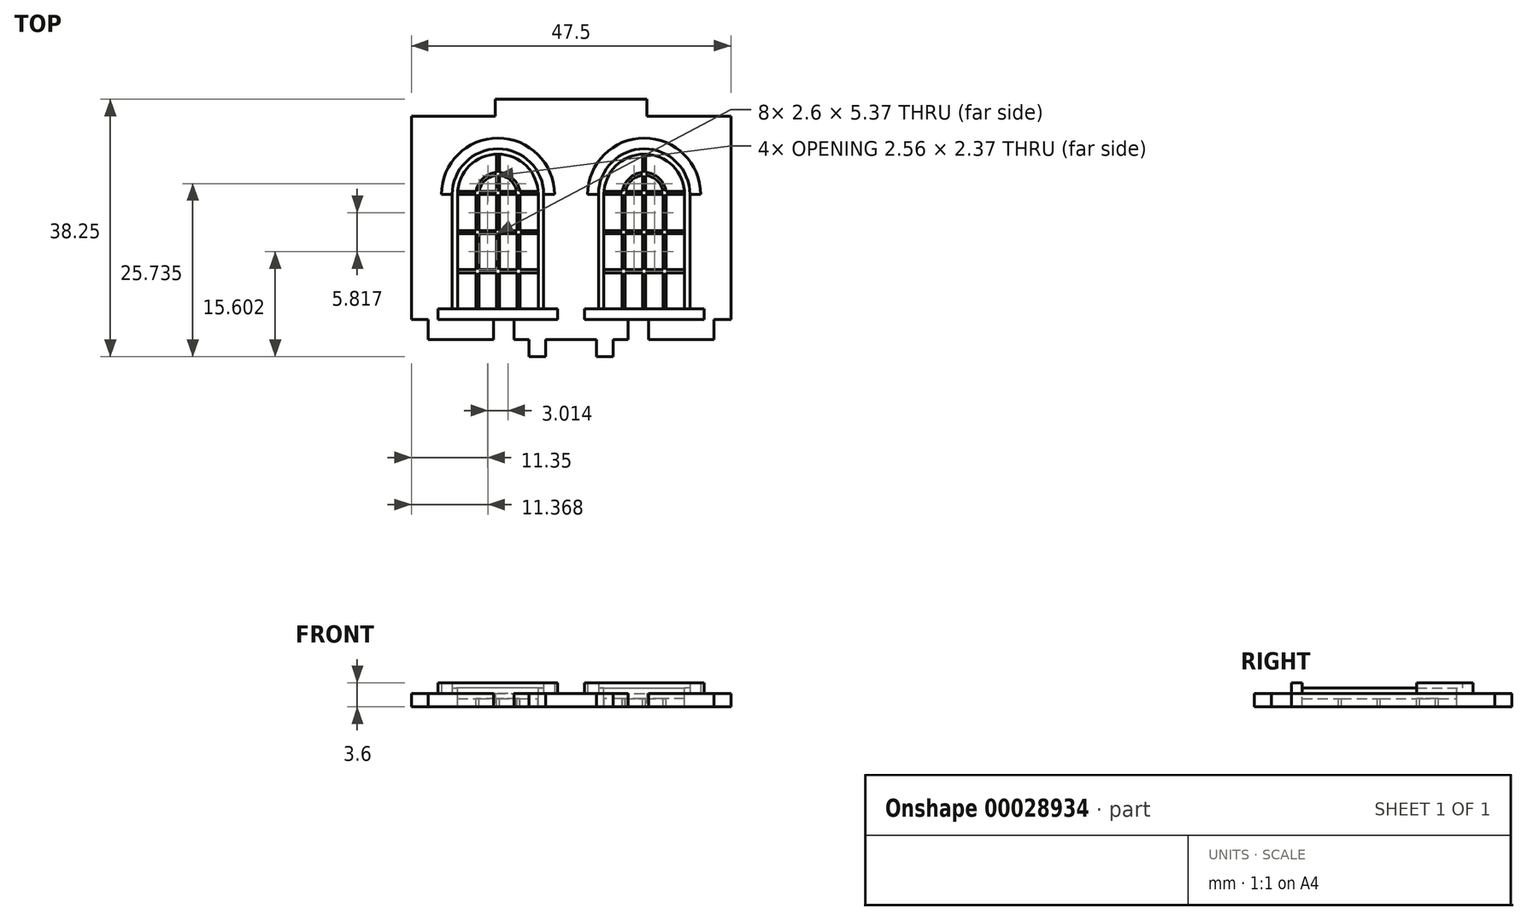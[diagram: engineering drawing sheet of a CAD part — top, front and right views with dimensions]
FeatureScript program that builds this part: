
annotation { "Feature Type Name" : "Feature", "Feature Type Description" : "" }
export const myFeature = defineFeature(function(context is Context, id is Id, definition is map)
    precondition{}
    {
        {
            var Q0;
            Q0=qCreatedBy(makeId("Top.planeOp"),FACE);
            var sketch = newSketch(context, id + "F0", { "sketchPlane" : qUnion([Q0])});
            skLineSegment(sketch, "E0.bottom", {"start": v(-8.5, -5.78) * mm, "end": v(-11.5, -5.78) * mm});
            skLineSegment(sketch, "E0.top", {"start": v(-11.25, 24.47) * mm, "end": v(-23.75, 24.47) * mm});
            skLineSegment(sketch, "E0.right", {"start": v(-23.75, -5.78) * mm, "end": v(-23.75, 24.47) * mm});
            skLineSegment(sketch, "E1.top", {"start": v(-11.25, 26.97) * mm, "end": v(0, 26.97) * mm});
            skLineSegment(sketch, "E1.left", {"start": v(-11.25, 24.47) * mm, "end": v(-11.25, 26.97) * mm});
            skLineSegment(sketch, "E1.right", {"start": v(0, -8.78) * mm, "end": v(0, 26.97) * mm});
            skLineSegment(sketch, "E2.top", {"start": v(-21.25, -8.78) * mm, "end": v(-11.5, -8.78) * mm});
            skLineSegment(sketch, "E2.left", {"start": v(-21.25, -5.78) * mm, "end": v(-21.25, -8.78) * mm});
            skLineSegment(sketch, "E2.right", {"start": v(-11.5, -5.78) * mm, "end": v(-11.5, -8.78) * mm});
            skLineSegment(sketch, "E3.top", {"start": v(-8.5, -8.78) * mm, "end": v(-6.25, -8.78) * mm});
            skLineSegment(sketch, "E3.left", {"start": v(-8.5, -5.78) * mm, "end": v(-8.5, -8.78) * mm});
            skLineSegment(sketch, "E4.top", {"start": v(-6.25, -11.28) * mm, "end": v(-3.75, -11.28) * mm});
            skLineSegment(sketch, "E4.left", {"start": v(-6.25, -8.78) * mm, "end": v(-6.25, -11.28) * mm});
            skLineSegment(sketch, "E4.right", {"start": v(-3.75, -8.78) * mm, "end": v(-3.75, -11.28) * mm});
            skLineSegment(sketch, "E5.trimOffspring", {"start": v(-3.75, -8.78) * mm, "end": v(0, -8.78) * mm});
            skLineSegment(sketch, "E6.trimOffspring", {"start": v(-21.25, -5.78) * mm, "end": v(-23.75, -5.78) * mm});
            skLineSegment(sketch, "E7.MirrorCS", {"start": v(11.25, 26.97) * mm, "end": v(0, 26.97) * mm});
            skLineSegment(sketch, "E8.MirrorCS", {"start": v(11.25, 24.47) * mm, "end": v(11.25, 26.97) * mm});
            skLineSegment(sketch, "E9.MirrorCS", {"start": v(11.25, 24.47) * mm, "end": v(23.75, 24.47) * mm});
            skLineSegment(sketch, "E10.MirrorCS", {"start": v(23.75, -5.78) * mm, "end": v(23.75, 24.47) * mm});
            skLineSegment(sketch, "E11.MirrorCS", {"start": v(21.25, -5.78) * mm, "end": v(23.75, -5.78) * mm});
            skLineSegment(sketch, "E12.MirrorCS", {"start": v(21.25, -5.78) * mm, "end": v(21.25, -8.78) * mm});
            skLineSegment(sketch, "E13.MirrorCS", {"start": v(21.25, -8.78) * mm, "end": v(11.5, -8.78) * mm});
            skLineSegment(sketch, "E14.MirrorCS", {"start": v(11.5, -5.78) * mm, "end": v(11.5, -8.78) * mm});
            skLineSegment(sketch, "E15.MirrorCS", {"start": v(8.5, -5.78) * mm, "end": v(11.5, -5.78) * mm});
            skLineSegment(sketch, "E16.MirrorCS", {"start": v(8.5, -5.78) * mm, "end": v(8.5, -8.78) * mm});
            skLineSegment(sketch, "E17.MirrorCS", {"start": v(8.5, -8.78) * mm, "end": v(6.25, -8.78) * mm});
            skLineSegment(sketch, "E18.MirrorCS", {"start": v(6.25, -8.78) * mm, "end": v(6.25, -11.28) * mm});
            skLineSegment(sketch, "E19.MirrorCS", {"start": v(6.25, -11.28) * mm, "end": v(3.75, -11.28) * mm});
            skLineSegment(sketch, "E20.MirrorCS", {"start": v(3.75, -8.78) * mm, "end": v(3.75, -11.28) * mm});
            skLineSegment(sketch, "E21.MirrorCS", {"start": v(3.75, -8.78) * mm, "end": v(0, -8.78) * mm});
            skSolve(sketch);
        }
        {
            var Q0;
            Q0=makeQuery(id+"F0.imprint","IMPRINT",FACE,{"disambiguationData":[TD([[makeQuery(id+"F0.imprint","IMPRINT",EDGE,{"derivedFrom":sQuery(id+"F0.wireOp",EDGE,"E0.bottom")}),-1.0]])]});
            extrude(context, id + "F1", {"entities" : qUnion([Q0]), "depth" : 2 * mm});
        }
        {
            var Q0;
            Q0=makeQuery(id+"F1.opExtrude","CAP_FACE",FACE,{"disambiguationData":[OSD([sQuery(id+"F0.wireOp",EDGE,"E0.bottom"),sQuery(id+"F0.wireOp",EDGE,"E0.top"),sQuery(id+"F0.wireOp",EDGE,"E0.right"),sQuery(id+"F0.wireOp",EDGE,"E1.top"),sQuery(id+"F0.wireOp",EDGE,"E1.left"),sQuery(id+"F0.wireOp",EDGE,"E2.top"),sQuery(id+"F0.wireOp",EDGE,"E2.left"),sQuery(id+"F0.wireOp",EDGE,"E2.right"),sQuery(id+"F0.wireOp",EDGE,"E3.top"),sQuery(id+"F0.wireOp",EDGE,"E3.left"),sQuery(id+"F0.wireOp",EDGE,"E4.top"),sQuery(id+"F0.wireOp",EDGE,"E4.left"),sQuery(id+"F0.wireOp",EDGE,"E4.right"),sQuery(id+"F0.wireOp",EDGE,"E5.trimOffspring"),sQuery(id+"F0.wireOp",EDGE,"E6.trimOffspring"),sQuery(id+"F0.wireOp",EDGE,"E7.MirrorCS"),sQuery(id+"F0.wireOp",EDGE,"E8.MirrorCS"),sQuery(id+"F0.wireOp",EDGE,"E9.MirrorCS"),sQuery(id+"F0.wireOp",EDGE,"E10.MirrorCS"),sQuery(id+"F0.wireOp",EDGE,"E11.MirrorCS"),sQuery(id+"F0.wireOp",EDGE,"E12.MirrorCS"),sQuery(id+"F0.wireOp",EDGE,"E13.MirrorCS"),sQuery(id+"F0.wireOp",EDGE,"E14.MirrorCS"),sQuery(id+"F0.wireOp",EDGE,"E15.MirrorCS"),sQuery(id+"F0.wireOp",EDGE,"E16.MirrorCS"),sQuery(id+"F0.wireOp",EDGE,"E17.MirrorCS"),sQuery(id+"F0.wireOp",EDGE,"E18.MirrorCS"),sQuery(id+"F0.wireOp",EDGE,"E19.MirrorCS"),sQuery(id+"F0.wireOp",EDGE,"E20.MirrorCS"),sQuery(id+"F0.wireOp",EDGE,"E21.MirrorCS")])],"isStart":false});
            var sketch = newSketch(context, id + "F2", { "sketchPlane" : qUnion([Q0])});
            skLineSegment(sketch, "E22.bottom", {"start": v(-19.75, -5.78) * mm, "end": v(-2, -5.78) * mm});
            skLineSegment(sketch, "E22.top", {"start": v(-19.75, -4.18) * mm, "end": v(-2, -4.18) * mm});
            skLineSegment(sketch, "E22.left", {"start": v(-19.75, -5.78) * mm, "end": v(-19.75, -4.18) * mm});
            skLineSegment(sketch, "E22.right", {"start": v(-2, -5.78) * mm, "end": v(-2, -4.18) * mm});
            skLineSegment(sketch, "E23", {"start": v(-16.87, -4.18) * mm, "end": v(-16.87, 1.19) * mm});
            skLineSegment(sketch, "E24", {"start": v(-4.87, -4.18) * mm, "end": v(-4.87, 12.82) * mm});
            skArc(sketch, "E25", {"start": v(-4.87, 12.82) * mm, "mid": v(-10.87, 18.82) * mm, "end": v(-16.88, 12.82) * mm});
            skLineSegment(sketch, "E26", {"start": v(-10.88, 12.82) * mm, "end": v(-10.87, 1.64) * mm, "construction": true});
            skLineSegment(sketch, "E27.0", {"start": v(-4.07, -4.18) * mm, "end": v(-4.08, 12.82) * mm});
            skArc(sketch, "E27.1", {"start": v(-4.08, 12.82) * mm, "mid": v(-10.88, 19.62) * mm, "end": v(-17.67, 12.82) * mm});
            skLineSegment(sketch, "E27.2", {"start": v(-17.67, -4.18) * mm, "end": v(-17.67, 12.82) * mm});
            skArc(sketch, "E28.0", {"start": v(-2.47, 12.82) * mm, "mid": v(-10.88, 21.22) * mm, "end": v(-19.28, 12.82) * mm});
            skLineSegment(sketch, "E29", {"start": v(-19.28, 12.82) * mm, "end": v(-17.67, 12.82) * mm});
            skLineSegment(sketch, "E30", {"start": v(-4.08, 12.82) * mm, "end": v(-2.47, 12.82) * mm});
            skLineSegment(sketch, "E31", {"start": v(-13.7, -4.18) * mm, "end": v(-13.7, 1.19) * mm});
            skLineSegment(sketch, "E32", {"start": v(-8.05, -4.18) * mm, "end": v(-8.05, 1.19) * mm});
            skArc(sketch, "E33", {"start": v(-8.09, 13.27) * mm, "mid": v(-8.96, 14.9) * mm, "end": v(-10.65, 15.64) * mm});
            skLineSegment(sketch, "E34.0", {"start": v(-7.6, -4.18) * mm, "end": v(-7.6, 1.19) * mm});
            skArc(sketch, "E34.1", {"start": v(-7.63, 13.27) * mm, "mid": v(-8.64, 15.22) * mm, "end": v(-10.65, 16.09) * mm});
            skLineSegment(sketch, "E34.2", {"start": v(-14.15, -4.18) * mm, "end": v(-14.15, 1.19) * mm});
            skLineSegment(sketch, "E35", {"start": v(-11.1, -4.18) * mm, "end": v(-11.1, 1.19) * mm});
            skLineSegment(sketch, "E36", {"start": v(-10.65, 18.82) * mm, "end": v(-10.65, 16.09) * mm});
            skLineSegment(sketch, "E37", {"start": v(-16.86, 13.27) * mm, "end": v(-14.12, 13.27) * mm});
            skLineSegment(sketch, "E38", {"start": v(-16.87, 12.82) * mm, "end": v(-14.15, 12.82) * mm});
            skLineSegment(sketch, "E39.bottom", {"start": v(-16.87, 7) * mm, "end": v(-14.15, 7) * mm});
            skLineSegment(sketch, "E39.top", {"start": v(-16.87, 7.46) * mm, "end": v(-14.15, 7.46) * mm});
            skLineSegment(sketch, "E40.bottom", {"start": v(-16.87, 1.64) * mm, "end": v(-14.15, 1.64) * mm});
            skLineSegment(sketch, "E40.top", {"start": v(-16.87, 1.19) * mm, "end": v(-14.15, 1.19) * mm});
            skLineSegment(sketch, "E41.trimOffspring", {"start": v(-16.87, 7) * mm, "end": v(-16.87, 12.82) * mm});
            skLineSegment(sketch, "E42.trimOffspring", {"start": v(-14.15, 7.46) * mm, "end": v(-14.15, 12.82) * mm});
            skLineSegment(sketch, "E43.trimOffspring", {"start": v(-13.7, 7.46) * mm, "end": v(-13.7, 12.82) * mm});
            skLineSegment(sketch, "E44.trimOffspring", {"start": v(-13.7, 7) * mm, "end": v(-11.1, 7) * mm});
            skLineSegment(sketch, "E45.trimOffspring", {"start": v(-13.7, 7.46) * mm, "end": v(-11.1, 7.46) * mm});
            skLineSegment(sketch, "E46.trimOffspring", {"start": v(-8.05, 7.46) * mm, "end": v(-8.05, 12.82) * mm});
            skLineSegment(sketch, "E47.trimOffspring", {"start": v(-7.6, 7) * mm, "end": v(-4.88, 7) * mm});
            skLineSegment(sketch, "E48.trimOffspring", {"start": v(-7.6, 7.46) * mm, "end": v(-7.6, 12.82) * mm});
            skLineSegment(sketch, "E49.trimOffspring", {"start": v(-7.6, 7.46) * mm, "end": v(-4.88, 7.46) * mm});
            skLineSegment(sketch, "E50.trimOffspring", {"start": v(-7.6, 12.82) * mm, "end": v(-4.88, 12.82) * mm});
            skLineSegment(sketch, "E51.trimOffspring", {"start": v(-7.63, 13.27) * mm, "end": v(-4.9, 13.27) * mm});
            skLineSegment(sketch, "E52.trimOffspring", {"start": v(-13.7, 12.82) * mm, "end": v(-11.1, 12.82) * mm});
            skLineSegment(sketch, "E53.trimOffspring", {"start": v(-13.66, 13.27) * mm, "end": v(-11.1, 13.27) * mm});
            skLineSegment(sketch, "E54.trimOffspring", {"start": v(-11.1, 13.27) * mm, "end": v(-11.1, 15.64) * mm});
            skLineSegment(sketch, "E55.trimOffspring", {"start": v(-10.65, 13.27) * mm, "end": v(-8.09, 13.27) * mm});
            skLineSegment(sketch, "E56.trimOffspring", {"start": v(-10.65, 12.82) * mm, "end": v(-10.65, 7.46) * mm});
            skLineSegment(sketch, "E57.trimOffspring", {"start": v(-10.65, 12.82) * mm, "end": v(-8.05, 12.82) * mm});
            skArc(sketch, "E58.trimOffspring", {"start": v(-11.1, 15.64) * mm, "mid": v(-12.8, 14.9) * mm, "end": v(-13.66, 13.27) * mm});
            skArc(sketch, "E59.trimOffspring", {"start": v(-11.1, 16.09) * mm, "mid": v(-13.1, 15.22) * mm, "end": v(-14.12, 13.27) * mm});
            skLineSegment(sketch, "E60.trimOffspring", {"start": v(-11.1, 16.09) * mm, "end": v(-11.1, 18.82) * mm});
            skLineSegment(sketch, "E61.trimOffspring", {"start": v(-10.65, 15.64) * mm, "end": v(-10.65, 13.27) * mm});
            skLineSegment(sketch, "E62.trimOffspring", {"start": v(-13.7, 1.64) * mm, "end": v(-13.7, 7) * mm});
            skLineSegment(sketch, "E63.trimOffspring", {"start": v(-13.7, 1.64) * mm, "end": v(-11.1, 1.64) * mm});
            skLineSegment(sketch, "E64.trimOffspring", {"start": v(-14.15, 1.64) * mm, "end": v(-14.15, 7) * mm});
            skLineSegment(sketch, "E65.trimOffspring", {"start": v(-13.7, 1.19) * mm, "end": v(-11.1, 1.19) * mm});
            skLineSegment(sketch, "E66.trimOffspring", {"start": v(-10.65, 1.19) * mm, "end": v(-10.65, -4.18) * mm});
            skLineSegment(sketch, "E67.trimOffspring", {"start": v(-11.1, 1.64) * mm, "end": v(-11.1, 7) * mm});
            skLineSegment(sketch, "E68.trimOffspring", {"start": v(-10.87, 1.19) * mm, "end": v(-10.87, -4.18) * mm, "construction": true});
            skLineSegment(sketch, "E69.trimOffspring", {"start": v(-10.65, 1.64) * mm, "end": v(-8.05, 1.64) * mm});
            skLineSegment(sketch, "E70.trimOffspring", {"start": v(-10.65, 1.19) * mm, "end": v(-8.05, 1.19) * mm});
            skLineSegment(sketch, "E71.trimOffspring", {"start": v(-7.6, 1.64) * mm, "end": v(-4.88, 1.64) * mm});
            skLineSegment(sketch, "E72.trimOffspring", {"start": v(-8.05, 1.64) * mm, "end": v(-8.05, 7) * mm});
            skLineSegment(sketch, "E73.trimOffspring", {"start": v(-7.6, 1.19) * mm, "end": v(-4.88, 1.19) * mm});
            skLineSegment(sketch, "E74.trimOffspring", {"start": v(-7.6, 1.64) * mm, "end": v(-7.6, 7) * mm});
            skLineSegment(sketch, "E75", {"start": v(-16.87, 7.46) * mm, "end": v(-16.87, 7) * mm});
            skLineSegment(sketch, "E76.trimOffspring", {"start": v(-16.87, 1.64) * mm, "end": v(-16.87, 7.46) * mm});
            skLineSegment(sketch, "E77", {"start": v(-16.87, 1.64) * mm, "end": v(-16.87, 1.19) * mm});
            skLineSegment(sketch, "E78.trimOffspring", {"start": v(-10.65, 7) * mm, "end": v(-10.65, 1.64) * mm});
            skLineSegment(sketch, "E79.trimOffspring", {"start": v(-10.65, 7.46) * mm, "end": v(-8.05, 7.46) * mm});
            skLineSegment(sketch, "E80.trimOffspring", {"start": v(-10.65, 7) * mm, "end": v(-8.05, 7) * mm});
            skLineSegment(sketch, "E81.trimOffspring", {"start": v(-11.1, 7.46) * mm, "end": v(-11.1, 12.82) * mm});
            skSolve(sketch);
        }
        {
            var Q0;
            {var subQ1=sQuery(id+"F2.wireOp",EDGE,"E37");Q0=makeQuery(id+"F2.imprint","IMPRINT",FACE,{"disambiguationData":[TD([[makeQuery(id+"F2.imprint","IMPRINT",EDGE,{"derivedFrom":subQ1}),1.0]])]});}
            var Q1;
            Q1=makeQuery(id+"F2.imprint","IMPRINT",FACE,{"disambiguationData":[TD([[makeQuery(id+"F2.imprint","IMPRINT",EDGE,{"derivedFrom":sQuery(id+"F2.wireOp",EDGE,"E53.trimOffspring")}),1.0]])]});
            var Q2;
            Q2=makeQuery(id+"F2.imprint","IMPRINT",FACE,{"disambiguationData":[TD([[makeQuery(id+"F2.imprint","IMPRINT",EDGE,{"derivedFrom":sQuery(id+"F2.wireOp",EDGE,"E34.1")}),-1.0]])]});
            var Q3;
            Q3=makeQuery(id+"F2.imprint","IMPRINT",FACE,{"disambiguationData":[TD([[makeQuery(id+"F2.imprint","IMPRINT",EDGE,{"derivedFrom":sQuery(id+"F2.wireOp",EDGE,"E33")}),1.0]])]});
            var Q4;
            Q4=makeQuery(id+"F2.imprint","IMPRINT",FACE,{"disambiguationData":[TD([[makeQuery(id+"F2.imprint","IMPRINT",EDGE,{"derivedFrom":sQuery(id+"F2.wireOp",EDGE,"E48.trimOffspring")}),-1.0]])]});
            var Q5;
            Q5=makeQuery(id+"F2.imprint","IMPRINT",FACE,{"disambiguationData":[TD([[makeQuery(id+"F2.imprint","IMPRINT",EDGE,{"derivedFrom":sQuery(id+"F2.wireOp",EDGE,"E46.trimOffspring")}),1.0]])]});
            var Q6;
            Q6=makeQuery(id+"F2.imprint","IMPRINT",FACE,{"disambiguationData":[TD([[makeQuery(id+"F2.imprint","IMPRINT",EDGE,{"derivedFrom":sQuery(id+"F2.wireOp",EDGE,"E43.trimOffspring")}),-1.0]])]});
            var Q7;
            Q7=makeQuery(id+"F2.imprint","IMPRINT",FACE,{"disambiguationData":[TD([[makeQuery(id+"F2.imprint","IMPRINT",EDGE,{"derivedFrom":sQuery(id+"F2.wireOp",EDGE,"E38")}),-1.0]])]});
            var Q8;
            {var subQ2=sQuery(id+"F2.wireOp",EDGE,"E39.bottom");Q8=makeQuery(id+"F2.imprint","IMPRINT",FACE,{"disambiguationData":[TD([[makeQuery(id+"F2.imprint","IMPRINT",EDGE,{"derivedFrom":subQ2}),-1.0]])]});}
            var Q9;
            Q9=makeQuery(id+"F2.imprint","IMPRINT",FACE,{"disambiguationData":[TD([[makeQuery(id+"F2.imprint","IMPRINT",EDGE,{"derivedFrom":sQuery(id+"F2.wireOp",EDGE,"E44.trimOffspring")}),-1.0]])]});
            var Q10;
            Q10=makeQuery(id+"F2.imprint","IMPRINT",FACE,{"disambiguationData":[TD([[makeQuery(id+"F2.imprint","IMPRINT",EDGE,{"derivedFrom":sQuery(id+"F2.wireOp",EDGE,"E69.trimOffspring")}),1.0]])]});
            var Q11;
            {var subQ1=sQuery(id+"F2.wireOp",EDGE,"E47.trimOffspring");Q11=makeQuery(id+"F2.imprint","IMPRINT",FACE,{"disambiguationData":[TD([[makeQuery(id+"F2.imprint","IMPRINT",EDGE,{"derivedFrom":subQ1}),-1.0]])]});}
            var Q12;
            {var subQ1=sQuery(id+"F2.wireOp",EDGE,"E34.0");Q12=makeQuery(id+"F2.imprint","IMPRINT",FACE,{"disambiguationData":[TD([[makeQuery(id+"F2.imprint","IMPRINT",EDGE,{"derivedFrom":subQ1}),-1.0]])]});}
            var Q13;
            {var subQ1=sQuery(id+"F2.wireOp",EDGE,"E32");Q13=makeQuery(id+"F2.imprint","IMPRINT",FACE,{"disambiguationData":[TD([[makeQuery(id+"F2.imprint","IMPRINT",EDGE,{"derivedFrom":subQ1}),1.0]])]});}
            var Q14;
            {var subQ1=sQuery(id+"F2.wireOp",EDGE,"E31");Q14=makeQuery(id+"F2.imprint","IMPRINT",FACE,{"disambiguationData":[TD([[makeQuery(id+"F2.imprint","IMPRINT",EDGE,{"derivedFrom":subQ1}),-1.0]])]});}
            var Q15;
            {var subQ1=sQuery(id+"F2.wireOp",EDGE,"E23");Q15=makeQuery(id+"F2.imprint","IMPRINT",FACE,{"disambiguationData":[TD([[makeQuery(id+"F2.imprint","IMPRINT",EDGE,{"derivedFrom":subQ1}),-1.0]])]});}
            extrude(context, id + "F3", {"entities" : qUnion([Q0, Q1, Q2, Q3, Q4, Q5, Q6, Q7, Q8, Q9, Q10, Q11, Q12, Q13, Q14, Q15]), "operationType" : NewBodyOperationType.REMOVE, "endBound" : BoundingType.THROUGH_ALL, "oppositeDirection" : true, "depth" : 25 * mm});
        }
        {
            var Q0;
            {var subQ10=sQuery(id+"F2.wireOp",EDGE,"E31");Q0=makeQuery(id+"F2.imprint","IMPRINT",FACE,{"disambiguationData":[TD([[makeQuery(id+"F2.imprint","IMPRINT",EDGE,{"derivedFrom":subQ10}),1.0]])]});}
            extrude(context, id + "F4", {"entities" : qUnion([Q0]), "operationType" : NewBodyOperationType.REMOVE, "oppositeDirection" : true, "depth" : (0.8) * mm});
        }
        {
            var Q0;
            {var subQ19=sQuery(id+"F2.wireOp",EDGE,"E23");Q0=makeQuery(id+"F2.imprint","IMPRINT",FACE,{"disambiguationData":[TD([[makeQuery(id+"F2.imprint","IMPRINT",EDGE,{"derivedFrom":subQ19}),1.0]])]});}
            extrude(context, id + "F5", {"entities" : qUnion([Q0]), "operationType" : NewBodyOperationType.ADD, "depth" : 0.8 * mm});
        }
        {
            var Q0;
            Q0=makeQuery(id+"F2.imprint","IMPRINT",FACE,{"disambiguationData":[TD([[makeQuery(id+"F2.imprint","IMPRINT",EDGE,{"derivedFrom":sQuery(id+"F2.wireOp",EDGE,"E27.1")}),-1.0]])]});
            var Q1;
            {var subQ6=sQuery(id+"F2.wireOp",EDGE,"E22.left");Q1=makeQuery(id+"F2.imprint","IMPRINT",FACE,{"disambiguationData":[TD([[makeQuery(id+"F2.imprint","IMPRINT",EDGE,{"derivedFrom":subQ6}),-1.0]])]});}
            extrude(context, id + "F6", {"entities" : qUnion([Q0, Q1]), "operationType" : NewBodyOperationType.ADD, "depth" : 1.6 * mm});
        }
        {
            var Q0;
            Q0=makeQuery(id+"F1.opExtrude","SWEPT_BODY",BODY,{"disambiguationData":[OSD([sQuery(id+"F0.wireOp",EDGE,"E0.bottom"),sQuery(id+"F0.wireOp",EDGE,"E0.top"),sQuery(id+"F0.wireOp",EDGE,"E0.right"),sQuery(id+"F0.wireOp",EDGE,"E1.top"),sQuery(id+"F0.wireOp",EDGE,"E1.left"),sQuery(id+"F0.wireOp",EDGE,"E1.right"),sQuery(id+"F0.wireOp",EDGE,"E2.top"),sQuery(id+"F0.wireOp",EDGE,"E2.left"),sQuery(id+"F0.wireOp",EDGE,"E2.right"),sQuery(id+"F0.wireOp",EDGE,"E3.top"),sQuery(id+"F0.wireOp",EDGE,"E3.left"),sQuery(id+"F0.wireOp",EDGE,"E4.top"),sQuery(id+"F0.wireOp",EDGE,"E4.left"),sQuery(id+"F0.wireOp",EDGE,"E4.right"),sQuery(id+"F0.wireOp",EDGE,"E5.trimOffspring"),sQuery(id+"F0.wireOp",EDGE,"E6.trimOffspring")])]});
            var Q1;
            Q1=qCreatedBy(makeId("Right.planeOp"),FACE);
            mirror(context, id + "F7", {"operationType" : NewBodyOperationType.ADD, "entities" : qUnion([Q0]), "mirrorPlane" : qUnion([Q1])});
        }
    });
